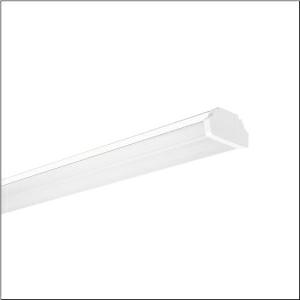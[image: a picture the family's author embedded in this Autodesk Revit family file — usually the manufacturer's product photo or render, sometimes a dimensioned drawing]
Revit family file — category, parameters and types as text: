
# Revit family: dus_r__31_gen_2_53bd812cv6c5d2_2f7a
name_source: partatom
category: Lighting Fixtures
units: mm (PartAtom-declared; Revit-internal decimal feet)

## family parameters
Cut with Voids When Loaded = No
Host = Face
Light Source = No
Part Type = Normal
Room Calculation Point = No
Round Connector Dimension = Use Diameter
Shared = No

## types (1)
- --- (1 x LED, 12660 lm, 68.5 W, 6500K)
    Apparent Load = 69 VA
    CIE Flux Codes = 47 80 95 93 100
    Color Rendering = 80
    Color Temperature = 6500K
    Default Elevation = 1800 mm
    Description = DUS® 31 Gen.2, luminaire insert, of sheet steel, coil coated, white, length: 1.535mm, width: 81mm, height: 90mm, 5x system unit, system units: 307mm, LED rated luminous flux: 12.660lm, light colour: 865, control gear: ON/OFF Multilumen, CLOi, with plug, 3-pole, with phase selection, mains connection: 220..240V, AC, 50/60Hz, start of lifetime: 69W, end of service life: 82W, through-wiring accessed according to module size, primary optical cover: cover, of PMMA, light emission: direct distribution, primary light characteristic: symmetric, protection rating (complete): IP20, protection rating (LED compartment): IP50, insulation class (complete): insulation class I (protective earthing), certification: CE, ENEC, VDE, UKCA, impact resistance: IK03, permissible ambient temperature for indoor applications: -35..+35°C, corresponds to IFS (International Featured Standards) requirements for safety and quality in the food industry, reducing of maximum allowable ambient temperature of 5°C with ceiling mounting, packaging unit: 1 piece
    Height = 95 mm
    Lamp = 1 x LED
    Lamp Light Flux = 12660 lm
    Lamp Power = 68.5 W
    Lamp count = 1
    Length = 1535 mm
    Luminous efficacy = 185 lm/W
    Manufacturer = Siteco
    ModVariant = No
    Model = 53BD812CV6C5D2
    Mounting Place = Ceiling
    Mounting Type = Pendant
    Number of Poles = 1
    OnlyDefault = Yes
    Power Factor = 1
    Product Name = DUS® 31 Gen.2
    Product group = luminaire insert
    ProductGroupID = 901
    Protection Class = Protection class I
    Protection Degree = IP 20
    RLX_Detail_Level = 1
    RLX_Emergency_Light_Flux = 0 lm
    RLX_Emergency_Type = 0
    RLX_Emergency_Type_DB = No
    RlxData = <blob elided: 29821 chars, md5=d8183a0a>
    Socket = socket
    Standby Power = 0 W
    System Light Flux = 12660 lm
    System Power = 69 W
    Type Comments = factory setting: luminous flux: 100 % | (A | C | E) | 161 mA
    Type Image = l_1319596.jpg
    URL = http://relux.com
    VarID = @adj_009987
    Voltage = 0 V
    Weight = 0.00 kg
    Width = 81 mm

## geometry (parser evidence)
native form markers: Blend x4, Sweep x12
no freeform markers — native parametric forms only
